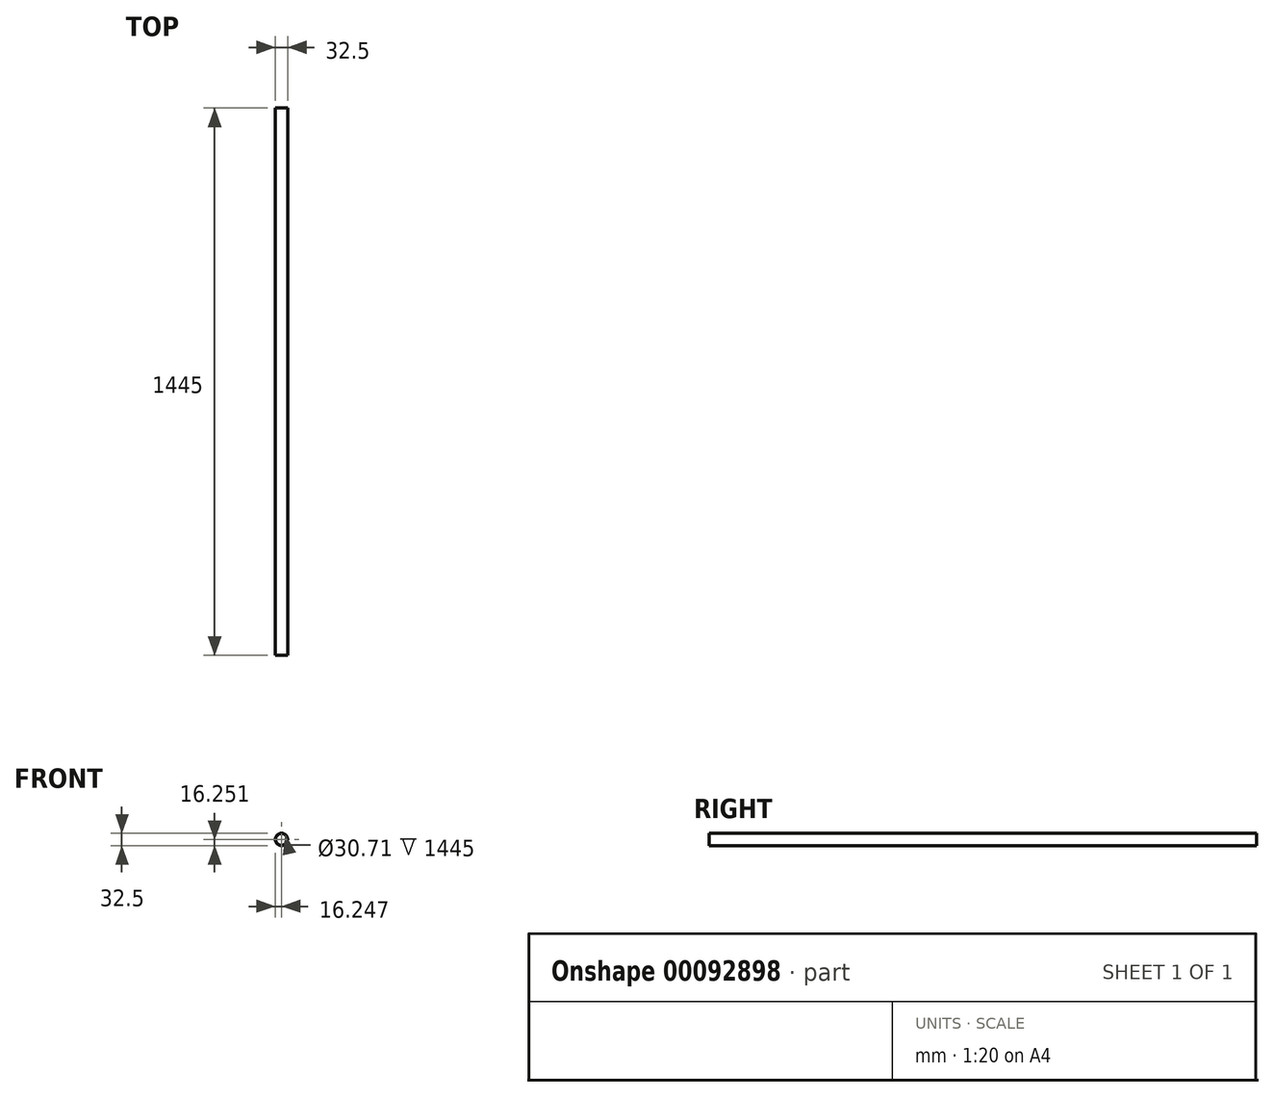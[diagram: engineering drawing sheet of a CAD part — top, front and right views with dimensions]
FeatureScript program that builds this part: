
annotation { "Feature Type Name" : "Feature", "Feature Type Description" : "" }
export const myFeature = defineFeature(function(context is Context, id is Id, definition is map)
    precondition{}
    {
        {
            var Q0;
            Q0=qCreatedBy(makeId("Front.planeOp"),FACE);
            var sketch = newSketch(context, id + "F0", { "sketchPlane" : qUnion([Q0])});
            skCircle(sketch, "E0", {"center": v(63.95, 69.96) * mm, "radius": 16.25 * mm});
            skCircle(sketch, "E1", {"center": v(63.95, 69.96) * mm, "radius": 15.35 * mm});
            skSolve(sketch);
        }
        {
            var Q0;
            Q0=makeQuery(id+"F0.imprint","IMPRINT",FACE,{"disambiguationData":[TD([[makeQuery(id+"F0.imprint","IMPRINT",EDGE,{"derivedFrom":sQuery(id+"F0.wireOp",EDGE,"E0")}),1.0]])]});
            extrude(context, id + "F1", {"entities" : qUnion([Q0]), "endBound" : BoundingType.SYMMETRIC, "depth" : 1445 * mm});
        }
    });
